# Revit family: WAGNER_Фильтр_воздушный
name_source: partatom
category: Оборудование
revit_build: Autodesk Revit 2017 (Build: 20170118_1100(x64)
units: mm (PartAtom-declared; Revit-internal decimal feet)

## family parameters
Всегда вертикально = Да
Заголовок OmniClass = Dust Collectors
На основе рабочей плоскости = Нет
Номер OmniClass = 23.70.30.24.17
Общий = Да
При загрузке вырезать с полостями = Нет
Размер круглого соединителя = Использовать диаметр
Тип детали = Нормальный
Точка расчета площади = Нет

## types (3) — shared parameters
ADSK_Версия Revit = Revit 2017
ADSK_Версия семейства = Версия 1
ADSK_Дата изменения = 08.07.20
ADSK_Единица измерения = шт.
ADSK_Завод-изготовитель = WAGNER
ADSK_Код изделия = -
ADSK_Материал = WAGNER_Корпус
ADSK_Размер_Высота = 151 мм
ADSK_Размер_Длина = 127 мм
ADSK_Размер_Ширина = 91 мм
COBie Category = Panel air filters
Masterformat Code = 23 01 30.51
Masterformat Title = HVAC Air-Distribution System Cleaning
OmniClass Code = 23-27 57 27
OmniClass Title = Air Filters
UNSPSC Code = 401615
UNSPSC Title = Filters
URL = www.wagner-russia.com
Uniclass Code = Pr_65_57_02_66
Uniclass Title = Panel air filters
bimon.ru = bimon.ru
Изготовитель = WAGNER

## per-type parameters (varying)
| type | WAGNER_Variation | WAGNER_Артикул | WAGNER_Название | WAGNER_Температурный режим. |
| Typ LF-AD-1/a | 2 | AD-10-1963 | Фильтр воздушный, 10 микрон | от -20℃ до +60℃ |
| Typ LF-AD/a | 1 | AD-10-1960 | Фильтр воздушный, 15 микрон | от -20℃ до +60℃ |
| Typ LF-AD-2/a | 3 | AD-10-1966 | Фильтр воздушный, 5 микрон | от -40℃ до +60℃ |

note: column(s) folded — value = type name in every type: ADSK_Марка, WAGNER_Тип

## geometry (parser evidence)
native form markers: Blend x2
no freeform markers — native parametric forms only
